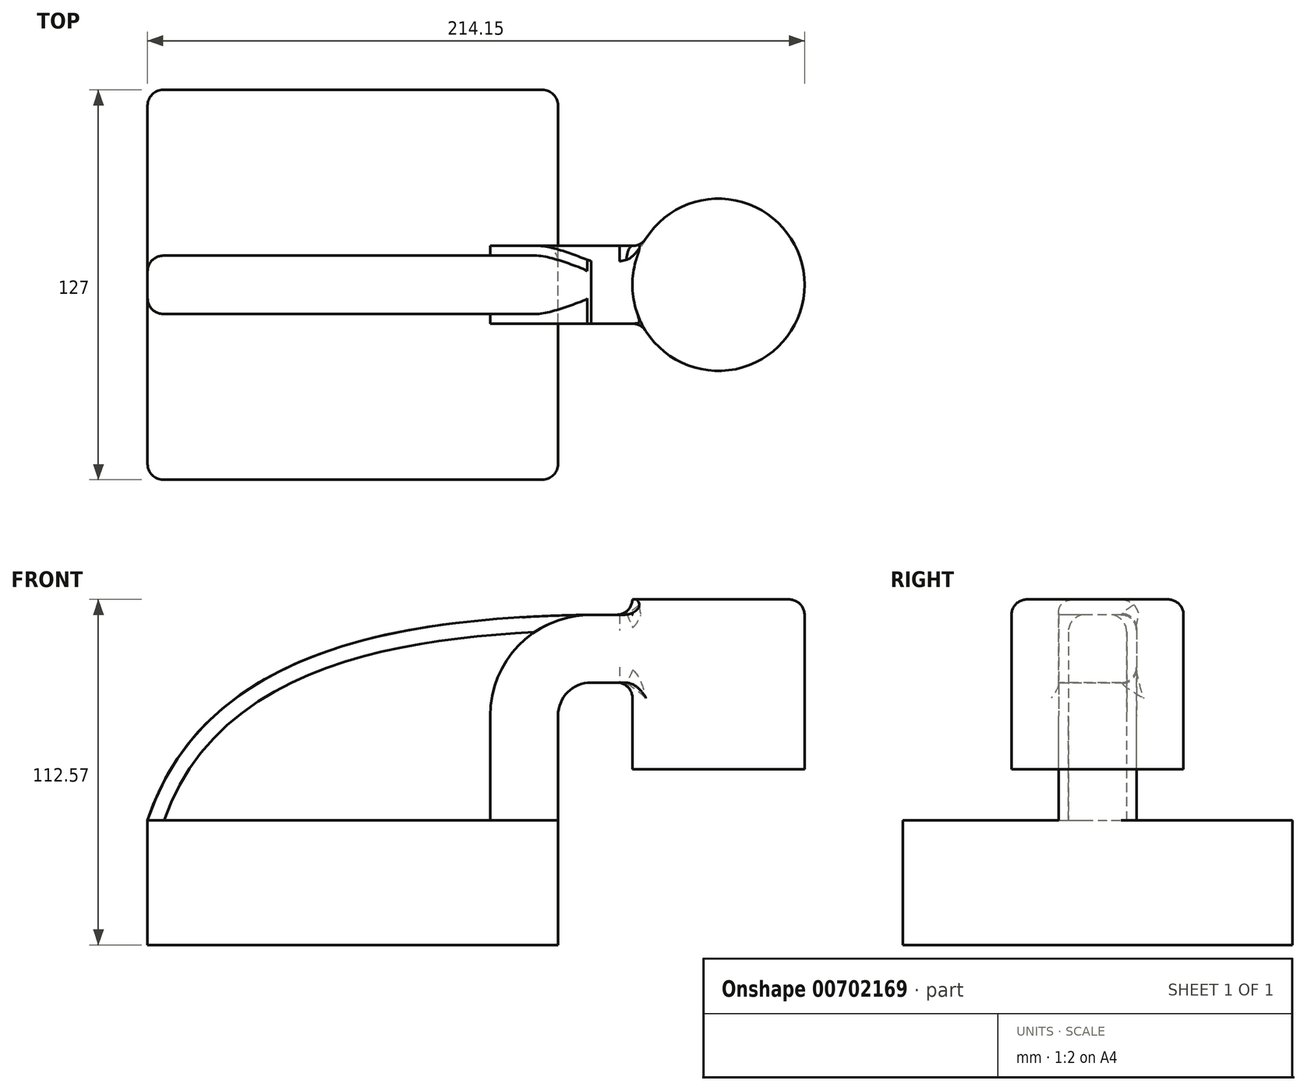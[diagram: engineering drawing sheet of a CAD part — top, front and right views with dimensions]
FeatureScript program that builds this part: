
annotation { "Feature Type Name" : "Feature", "Feature Type Description" : "" }
export const myFeature = defineFeature(function(context is Context, id is Id, definition is map)
    precondition{}
    {
        {
            var Q0;
            Q0=qCreatedBy(makeId("Front.planeOp"),FACE);
            var sketch = newSketch(context, id + "F0", { "sketchPlane" : qUnion([Q0])});
            skLineSegment(sketch, "E0.bottom", {"start": v(66.9, 20.28) * mm, "end": v(-66.9, 20.28) * mm});
            skLineSegment(sketch, "E0.top", {"start": v(66.9, -20.28) * mm, "end": v(-66.9, -20.28) * mm});
            skLineSegment(sketch, "E0.left", {"start": v(66.9, 20.28) * mm, "end": v(66.9, -20.28) * mm});
            skLineSegment(sketch, "E0.right", {"start": v(-66.9, 20.28) * mm, "end": v(-66.9, -20.28) * mm});
            skPoint(sketch, "E0.middle", {"position": v(0, 0) * mm});
            skLineSegment(sketch, "E1.bottom", {"start": v(147.25, 92.3) * mm, "end": v(91.15, 92.3) * mm});
            skLineSegment(sketch, "E1.top", {"start": v(147.25, 36.95) * mm, "end": v(91.15, 36.95) * mm});
            skLineSegment(sketch, "E1.left", {"start": v(147.25, 92.3) * mm, "end": v(147.25, 36.95) * mm});
            skLineSegment(sketch, "E1.right", {"start": v(91.15, 92.3) * mm, "end": v(91.15, 36.95) * mm});
            skPoint(sketch, "E1.middle", {"position": v(119.2, 64.62) * mm});
            skLineSegment(sketch, "E2", {"start": v(66.9, 20.28) * mm, "end": v(66.9, 54.39) * mm});
            skArc(sketch, "E3", {"start": v(66.9, 54.39) * mm, "mid": v(70.06, 62.03) * mm, "end": v(77.7, 65.2) * mm});
            skLineSegment(sketch, "E4", {"start": v(77.7, 65.2) * mm, "end": v(113.14, 65.2) * mm});
            skLineSegment(sketch, "E5.0", {"start": v(77.7, 87.3) * mm, "end": v(113.14, 87.3) * mm});
            skArc(sketch, "E5.1", {"start": v(44.8, 54.39) * mm, "mid": v(54.44, 77.66) * mm, "end": v(77.7, 87.3) * mm});
            skLineSegment(sketch, "E5.2", {"start": v(44.8, 20.28) * mm, "end": v(44.8, 54.39) * mm});
            skFitSpline(sketch, "E6", {"points": [v(-66.9, 20.28) * mm, v(77.7, 87.3) * mm], "startDerivative": vector(57.69, 177.33) * mm, "endDerivative": vector(163.57, 2.95) * mm});
            skLineSegment(sketch, "E7", {"start": v(119.2, 36.95) * mm, "end": v(119.2, 92.3) * mm});
            skSolve(sketch);
        }
        {
            var Q0;
            Q0=makeQuery(id+"F0.imprint","IMPRINT",FACE,{"disambiguationData":[TD([[makeQuery(id+"F0.imprint","IMPRINT",EDGE,{"derivedFrom":sQuery(id+"F0.wireOp",EDGE,"E0.bottom")}),1.0]])]});
            extrude(context, id + "F1", {"entities" : qUnion([Q0]), "endBound" : BoundingType.SYMMETRIC, "depth" : 127 * mm, "offsetDistance" : 25.4 * mm});
        }
        {
            var Q0;
            {var subQ1=sQuery(id+"F0.wireOp",EDGE,"E2");Q0=makeQuery(id+"F0.imprint","IMPRINT",FACE,{"disambiguationData":[TD([[makeQuery(id+"F0.imprint","IMPRINT",EDGE,{"derivedFrom":subQ1}),1.0]])]});}
            extrude(context, id + "F2", {"entities" : qUnion([Q0]), "operationType" : NewBodyOperationType.ADD, "endBound" : BoundingType.SYMMETRIC, "depth" : 25.4 * mm, "offsetDistance" : 25.4 * mm});
        }
        {
            var Q0;
            {var subQ3=sQuery(id+"F0.wireOp",EDGE,"E5.2");Q0=makeQuery(id+"F0.imprint","IMPRINT",FACE,{"disambiguationData":[TD([[makeQuery(id+"F0.imprint","IMPRINT",EDGE,{"derivedFrom":subQ3}),1.0]])]});}
            extrude(context, id + "F3", {"entities" : qUnion([Q0]), "operationType" : NewBodyOperationType.ADD, "endBound" : BoundingType.SYMMETRIC, "depth" : 19.05 * mm, "offsetDistance" : 25.4 * mm});
        }
        {
            var Q0;
            {var subQ0=sQuery(id+"F0.wireOp",EDGE,"E1.left");Q0=makeQuery(id+"F0.imprint","IMPRINT",FACE,{"disambiguationData":[TD([[makeQuery(id+"F0.imprint","IMPRINT",EDGE,{"derivedFrom":subQ0}),-1.0]])]});}
            var Q1;
            Q1=sQuery(id+"F0.wireOp",EDGE,"E7");
            revolve(context, id + "F4", {"operationType" : NewBodyOperationType.ADD, "entities" : qUnion([Q0]), "axis" : qUnion([Q1]), "revolveType" : RevolveType.FULL});
        }
        {
            var Q0;
            Q0=makeQuery(id+"F1.opExtrude","CAP_EDGE",EDGE,{"disambiguationData":[OSD([sQuery(id+"F0.wireOp",EDGE,"E0.left")])],"isStart":false});
            var Q1;
            Q1=makeQuery(id+"F1.opExtrude","CAP_EDGE",EDGE,{"disambiguationData":[OSD([sQuery(id+"F0.wireOp",EDGE,"E0.right")])],"isStart":false});
            var Q2;
            Q2=makeQuery(id+"F1.opExtrude","CAP_EDGE",EDGE,{"disambiguationData":[OSD([sQuery(id+"F0.wireOp",EDGE,"E0.right")])],"isStart":true});
            var Q3;
            Q3=makeQuery(id+"F1.opExtrude","CAP_EDGE",EDGE,{"disambiguationData":[OSD([sQuery(id+"F0.wireOp",EDGE,"E0.left")])],"isStart":true});
            fillet(context, id + "F5", {"entities" : qUnion([Q0, Q1, Q2, Q3]), "radius" : 5.08 * mm, "tangentPropagation" : true, "allowEdgeOverflow" : false});
        }
        {
            var Q0;
            Q0=makeQuery(id+"F3.opExtrude","CAP_EDGE",EDGE,{"disambiguationData":[OSD([sQuery(id+"F0.wireOp",EDGE,"E6")])],"isStart":false});
            var Q1;
            Q1=makeQuery(id+"F3.opExtrude","CAP_EDGE",EDGE,{"disambiguationData":[OSD([sQuery(id+"F0.wireOp",EDGE,"E6")])],"isStart":true});
            fillet(context, id + "F6", {"entities" : qUnion([Q0, Q1]), "radius" : 5.08 * mm, "tangentPropagation" : true, "allowEdgeOverflow" : false});
        }
        {
            var Q0;
            Q0=makeQuery(id+"F2.opExtrude","SWEPT_FACE",FACE,{"disambiguationData":[OSD([sQuery(id+"F0.wireOp",EDGE,"E1.right")])]});
            extrude(context, id + "F7", {"entities" : qUnion([Q0]), "depth" : 25.4 * mm, "offsetDistance" : 25.4 * mm});
        }
        {
            var Q0;
            Q0=makeQuery(id+"F4.opRevolve","SWEPT_BODY",BODY,{"disambiguationData":[OSD([sQuery(id+"F0.wireOp",EDGE,"E1.bottom"),sQuery(id+"F0.wireOp",EDGE,"E1.top"),sQuery(id+"F0.wireOp",EDGE,"E1.left"),sQuery(id+"F0.wireOp",EDGE,"E7")])]});
            var Q1;
            Q1=makeQuery(id+"F7.opExtrude","SWEPT_BODY",BODY,{"disambiguationData":[OSD([sQuery(id+"F0.wireOp",EDGE,"E1.right")])]});
            booleanBodies(context, id + "F8", {"operationType" : BooleanOperationType.UNION, "tools" : qUnion([Q0, Q1])});
        }
        {
            var Q0;
            Q0=makeQuery(id+"F4.opRevolve","SWEPT_BODY",BODY,{"disambiguationData":[OSD([sQuery(id+"F0.wireOp",EDGE,"E1.bottom"),sQuery(id+"F0.wireOp",EDGE,"E1.top"),sQuery(id+"F0.wireOp",EDGE,"E1.left"),sQuery(id+"F0.wireOp",EDGE,"E7")])]});
            var Q1;
            Q1=makeQuery(id+"F1.opExtrude","SWEPT_BODY",BODY,{"disambiguationData":[OSD([sQuery(id+"F0.wireOp",EDGE,"E0.bottom"),sQuery(id+"F0.wireOp",EDGE,"E0.top"),sQuery(id+"F0.wireOp",EDGE,"E0.left"),sQuery(id+"F0.wireOp",EDGE,"E0.right")])]});
            booleanBodies(context, id + "F9", {"operationType" : BooleanOperationType.UNION, "tools" : qUnion([Q0, Q1])});
        }
        {
            var Q0;
            {var subQ0=sQuery(id+"F0.wireOp",EDGE,"E1.right");Q0=makeQuery(id+"F8.opBoolean","INTERSECT",EDGE,{"derivedFrom":[makeQuery(id+"F4.opRevolve","SWEPT_FACE",FACE,{"disambiguationData":[OSD([sQuery(id+"F0.wireOp",EDGE,"E1.left")])]}),makeQuery(id+"F7.opExtrude","SWEPT_FACE",FACE,{"disambiguationData":[OSD([subQ0]),TDD([makeQuery(id+"F2.opExtrude","CAP_EDGE",EDGE,{"disambiguationData":[OSD([subQ0])],"isStart":false})])]})]});}
            var Q1;
            {var subQ0=sQuery(id+"F0.wireOp",EDGE,"E1.right");Q1=makeQuery(id+"F8.opBoolean","INTERSECT",EDGE,{"derivedFrom":[makeQuery(id+"F4.opRevolve","SWEPT_FACE",FACE,{"disambiguationData":[OSD([sQuery(id+"F0.wireOp",EDGE,"E1.left")])]}),makeQuery(id+"F7.opExtrude","SWEPT_FACE",FACE,{"disambiguationData":[OSD([subQ0]),TDD([makeQuery(id+"F2.opExtrude","CAP_EDGE",EDGE,{"disambiguationData":[OSD([subQ0])],"isStart":true})])]})]});}
            fillet(context, id + "F10", {"entities" : qUnion([Q0, Q1]), "radius" : 5.08 * mm, "tangentPropagation" : true, "allowEdgeOverflow" : false});
        }
        {
            var Q0;
            {var subQ0=makeQuery(id+"F7.opExtrude","SWEPT_FACE",FACE,{"disambiguationData":[OSD([sQuery(id+"F0.wireOp",EDGE,"E1.right"),sQuery(id+"F0.wireOp",EDGE,"E5.0")])]});var subQ1=makeQuery(id+"F4.opRevolve","SWEPT_FACE",FACE,{"disambiguationData":[OSD([sQuery(id+"F0.wireOp",EDGE,"E1.left")])]});Q0=makeQuery(id+"F9.opBoolean","MERGE",EDGE,{"derivedFrom":[makeQuery(id+"F8.opBoolean","INTERSECT",EDGE,{"disambiguationData":[OD(0.0)],"derivedFrom":[subQ1,subQ0]}),makeQuery(id+"F8.opBoolean","INTERSECT",EDGE,{"disambiguationData":[OD(1.0)],"derivedFrom":[subQ1,subQ0]})]});}
            var Q1;
            {var subQ0=makeQuery(id+"F7.opExtrude","SWEPT_FACE",FACE,{"disambiguationData":[OSD([sQuery(id+"F0.wireOp",EDGE,"E1.right"),sQuery(id+"F0.wireOp",EDGE,"E4")])]});var subQ1=makeQuery(id+"F4.opRevolve","SWEPT_FACE",FACE,{"disambiguationData":[OSD([sQuery(id+"F0.wireOp",EDGE,"E1.left")])]});Q1=makeQuery(id+"F9.opBoolean","MERGE",EDGE,{"derivedFrom":[makeQuery(id+"F8.opBoolean","INTERSECT",EDGE,{"disambiguationData":[OD(0.0)],"derivedFrom":[subQ1,subQ0]}),makeQuery(id+"F8.opBoolean","INTERSECT",EDGE,{"disambiguationData":[OD(1.0)],"derivedFrom":[subQ1,subQ0]})]});}
            fillet(context, id + "F11", {"entities" : qUnion([Q0, Q1]), "radius" : 5.08 * mm, "tangentPropagation" : true, "allowEdgeOverflow" : false});
        }
        {
            var Q0;
            {var subQ0=sQuery(id+"F0.wireOp",EDGE,"E1.right");var subQ1=sQuery(id+"F0.wireOp",EDGE,"E1.left");var subQ2=makeQuery(id+"F4.opRevolve","SWEPT_FACE",FACE,{"disambiguationData":[OSD([subQ1])]});var subQ3=makeQuery(id+"F7.opExtrude","SWEPT_FACE",FACE,{"disambiguationData":[OSD([subQ0,sQuery(id+"F0.wireOp",EDGE,"E5.0")])]});Q0=makeQuery(id+"F11.opFillet","BLEND_EDGE",EDGE,{"blendedFrom":[makeQuery(id+"F9.opBoolean","MERGE",EDGE,{"derivedFrom":[makeQuery(id+"F8.opBoolean","INTERSECT",EDGE,{"disambiguationData":[OD(0.0)],"derivedFrom":[subQ2,subQ3]}),makeQuery(id+"F8.opBoolean","INTERSECT",EDGE,{"disambiguationData":[OD(1.0)],"derivedFrom":[subQ2,subQ3]})]}),makeQuery(id+"F10.opFillet","BLEND_FACE",FACE,{"disambiguationData":[OSD([subQ1,subQ0]),TDD([makeQuery(id+"F8.opBoolean","INTERSECT",EDGE,{"derivedFrom":[subQ2,makeQuery(id+"F7.opExtrude","SWEPT_FACE",FACE,{"disambiguationData":[OSD([subQ0]),TDD([makeQuery(id+"F2.opExtrude","CAP_EDGE",EDGE,{"disambiguationData":[OSD([subQ0])],"isStart":true})])]})]})])]})],"blendedInto":[makeQuery(id+"F10.opFillet","BLEND_FACE",FACE,{"disambiguationData":[OSD([subQ1,subQ0]),TDD([makeQuery(id+"F8.opBoolean","INTERSECT",EDGE,{"derivedFrom":[subQ2,makeQuery(id+"F7.opExtrude","SWEPT_FACE",FACE,{"disambiguationData":[OSD([subQ0]),TDD([makeQuery(id+"F2.opExtrude","CAP_EDGE",EDGE,{"disambiguationData":[OSD([subQ0])],"isStart":true})])]})]})])]})]});}
            var Q1;
            {var subQ0=sQuery(id+"F0.wireOp",EDGE,"E1.right");var subQ1=sQuery(id+"F0.wireOp",EDGE,"E1.left");var subQ2=makeQuery(id+"F4.opRevolve","SWEPT_FACE",FACE,{"disambiguationData":[OSD([subQ1])]});var subQ3=makeQuery(id+"F7.opExtrude","SWEPT_FACE",FACE,{"disambiguationData":[OSD([subQ0,sQuery(id+"F0.wireOp",EDGE,"E4")])]});Q1=makeQuery(id+"F11.opFillet","BLEND_EDGE",EDGE,{"blendedFrom":[makeQuery(id+"F9.opBoolean","MERGE",EDGE,{"derivedFrom":[makeQuery(id+"F8.opBoolean","INTERSECT",EDGE,{"disambiguationData":[OD(0.0)],"derivedFrom":[subQ2,subQ3]}),makeQuery(id+"F8.opBoolean","INTERSECT",EDGE,{"disambiguationData":[OD(1.0)],"derivedFrom":[subQ2,subQ3]})]}),makeQuery(id+"F10.opFillet","BLEND_FACE",FACE,{"disambiguationData":[OSD([subQ1,subQ0]),TDD([makeQuery(id+"F8.opBoolean","INTERSECT",EDGE,{"derivedFrom":[subQ2,makeQuery(id+"F7.opExtrude","SWEPT_FACE",FACE,{"disambiguationData":[OSD([subQ0]),TDD([makeQuery(id+"F2.opExtrude","CAP_EDGE",EDGE,{"disambiguationData":[OSD([subQ0])],"isStart":true})])]})]})])]})],"blendedInto":[makeQuery(id+"F10.opFillet","BLEND_FACE",FACE,{"disambiguationData":[OSD([subQ1,subQ0]),TDD([makeQuery(id+"F8.opBoolean","INTERSECT",EDGE,{"derivedFrom":[subQ2,makeQuery(id+"F7.opExtrude","SWEPT_FACE",FACE,{"disambiguationData":[OSD([subQ0]),TDD([makeQuery(id+"F2.opExtrude","CAP_EDGE",EDGE,{"disambiguationData":[OSD([subQ0])],"isStart":true})])]})]})])]})]});}
            fillet(context, id + "F12", {"entities" : qUnion([Q0, Q1]), "radius" : 5.08 * mm, "tangentPropagation" : true, "allowEdgeOverflow" : false});
        }
    });
